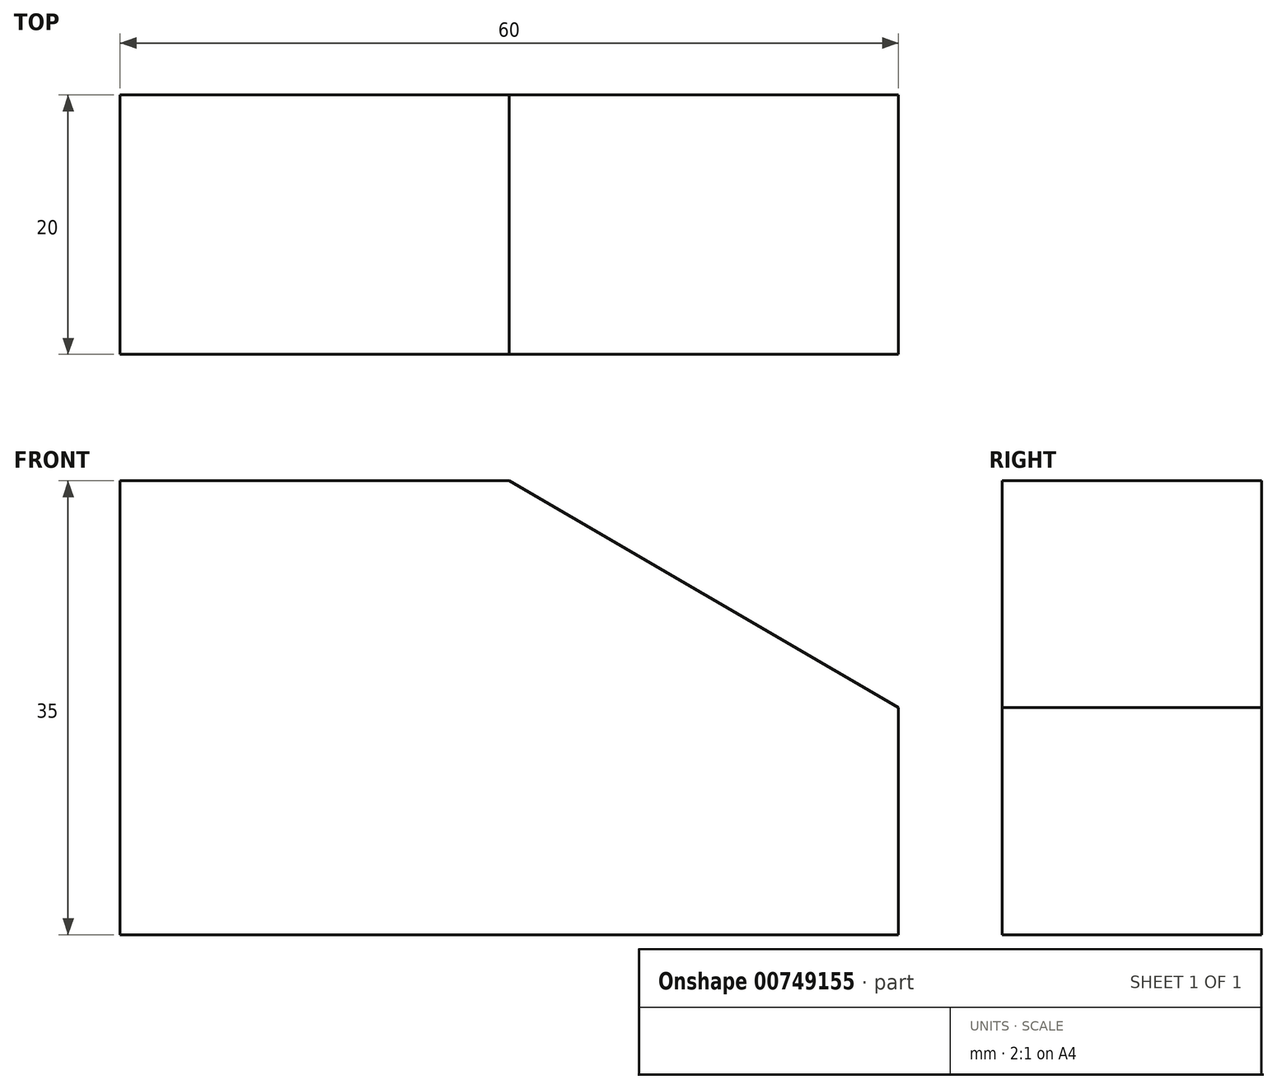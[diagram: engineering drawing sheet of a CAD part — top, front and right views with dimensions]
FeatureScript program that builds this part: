
annotation { "Feature Type Name" : "Feature", "Feature Type Description" : "" }
export const myFeature = defineFeature(function(context is Context, id is Id, definition is map)
    precondition{}
    {
        {
            var Q0;
            Q0=qCreatedBy(makeId("Front.planeOp"),FACE);
            var sketch = newSketch(context, id + "F0", { "sketchPlane" : qUnion([Q0])});
            skLineSegment(sketch, "E0", {"start": v(0, 35) * mm, "end": v(0, 0) * mm});
            skLineSegment(sketch, "E1", {"start": v(0, 0) * mm, "end": v(60, 0) * mm});
            skLineSegment(sketch, "E2", {"start": v(60, 0) * mm, "end": v(60, 17.5) * mm});
            skLineSegment(sketch, "E3", {"start": v(30, 35) * mm, "end": v(60, 17.5) * mm});
            skLineSegment(sketch, "E4", {"start": v(30, 35) * mm, "end": v(0, 35) * mm});
            skSolve(sketch);
        }
        {
            var Q0;
            Q0=makeQuery(id+"F0.imprint","IMPRINT",FACE,{"disambiguationData":[TD([[makeQuery(id+"F0.imprint","IMPRINT",EDGE,{"derivedFrom":sQuery(id+"F0.wireOp",EDGE,"E0")}),1.0]])]});
            extrude(context, id + "F1", {"entities" : qUnion([Q0]), "depth" : 20 * mm, "offsetDistance" : 25 * mm});
        }
    });
